# Revit family: Faucet-Lavatory-KOHLER-ALEO-K-72312AR_1
name_source: partatom
category: Plumbing Fixtures
revit_build: Autodesk Revit 2017 (Build: 20160225_1515(x64)
units: mm (PartAtom-declared; Revit-internal decimal feet)

## family parameters
Cut with Voids When Loaded = No
Host = Face
OmniClass Number = 23.31.11.00
OmniClass Title = Faucets
Part Type = Normal
Room Calculation Point = No
Round Connector Dimension = Use Diameter
Shared = No

## types (2) — shared parameters
ADA Compliant = No
Assembly Code = D2010
CW Connection = Yes
Cold Water Inlet = Cold Water Inlet
Date Modified = 09/24/2020
Default Elevation = 36"
Finish = Kohler-Metal-CP-Polished_Chrome
Flow Rate = 1 GPM
HW Connection = Yes
Handle Clearance = 3 13/16"
Height = 5 9/16"
Hot Water Inlet = Hot Water Inlet
Length = 4 1/8"
Manufacturer = KOHLER Co.
Master Format 2014 = 22 41 39
Master Format 2014 Name = Residential Faucets, Supplies, and Trim
Material = Premium Metal Construction
Pressure = 60.00 psi
Product Name = Aleo
Spout Reach = 4 1/8"
URL = https://la.kohler.com
Vent Connection = No
Waste Connection = No
Waste Water Outlet = Waste Water Outlet
WaterSense Certified = No
Width = 2"

## per-type parameters (varying)
| type | Description | Drain Included | Model | Type |
| With Drain, CP-Polished Chrome | Single-control  Basin Mixer with Drain | Yes | K-72312AR-4-CP | 1 |
| Without Drain, CP-Polished Chrome | Single-control  Basin Mixer without Drain | No | K-72312AR-4ND-CP | 2 |

## geometry (parser evidence)
native form markers: Sweep x5
no freeform markers — native parametric forms only
